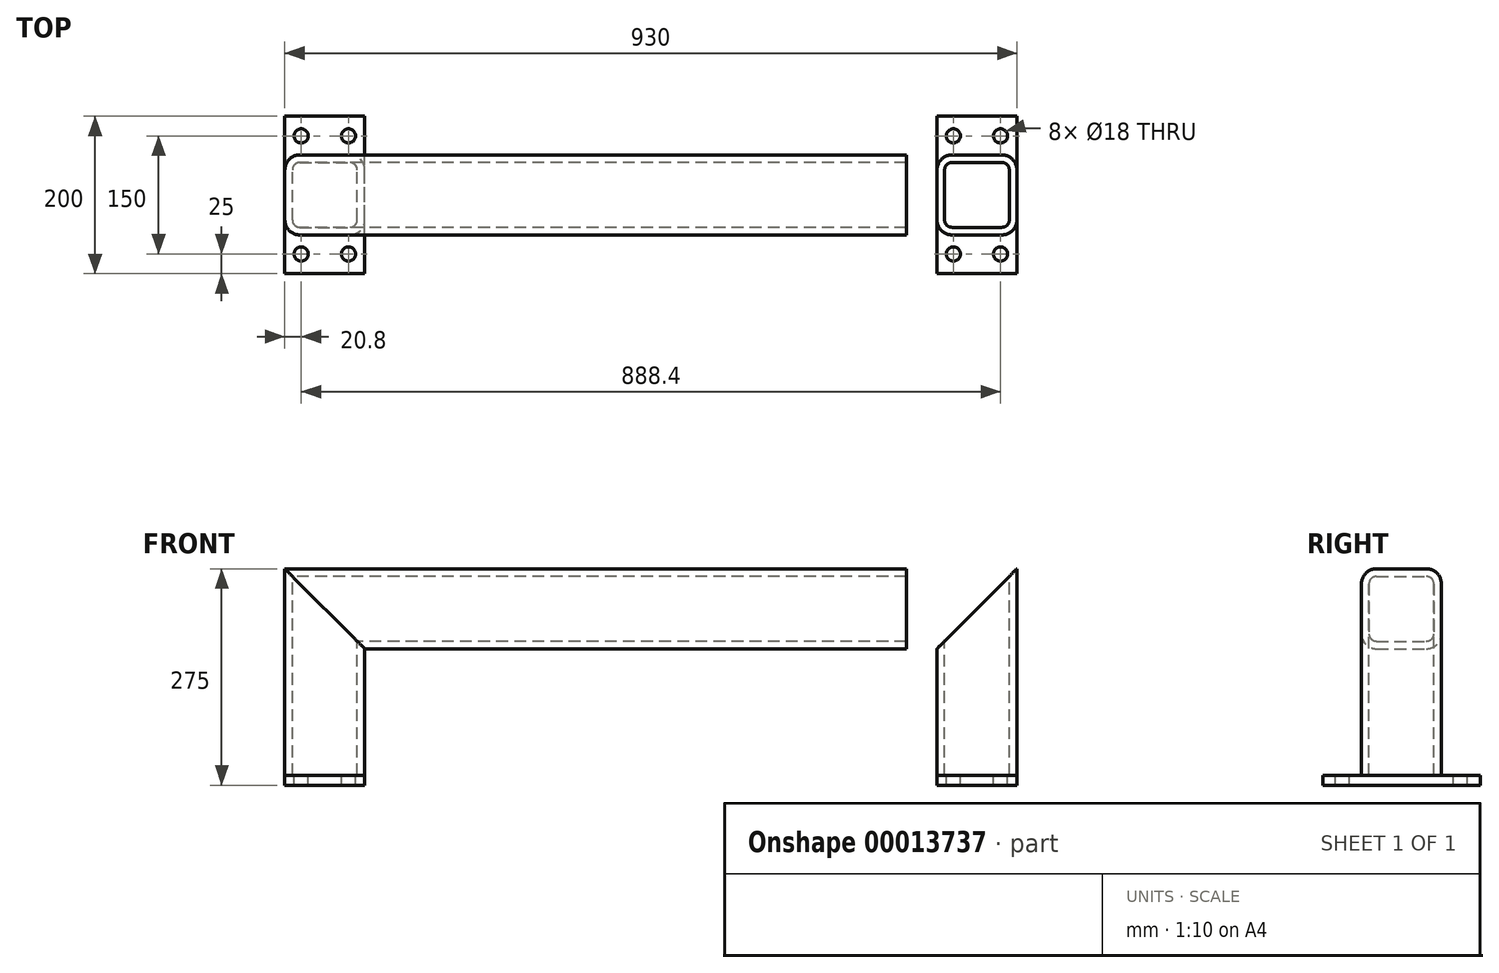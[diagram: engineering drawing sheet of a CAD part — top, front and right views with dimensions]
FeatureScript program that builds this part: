
annotation { "Feature Type Name" : "Feature", "Feature Type Description" : "" }
export const myFeature = defineFeature(function(context is Context, id is Id, definition is map)
    precondition{}
    {
        {
            var Q0;
            Q0=qCreatedBy(makeId("Right.planeOp"),FACE);
            var sketch = newSketch(context, id + "F0", { "sketchPlane" : qUnion([Q0])});
            skLineSegment(sketch, "E0.rect.bottom", {"start": v(-31.8, 50.8) * mm, "end": v(31.8, 50.8) * mm});
            skLineSegment(sketch, "E0.rect.top", {"start": v(-31.8, -50.8) * mm, "end": v(31.8, -50.8) * mm});
            skLineSegment(sketch, "E0.rect.left", {"start": v(-50.8, 31.8) * mm, "end": v(-50.8, -31.8) * mm});
            skLineSegment(sketch, "E0.rect.right", {"start": v(50.8, 31.8) * mm, "end": v(50.8, -31.8) * mm});
            skPoint(sketch, "E0.rect.middle", {"position": v(0, 0) * mm});
            skPoint(sketch, "E1.visualSharp", {"position": v(-50.8, 50.8) * mm});
            skArc(sketch, "E1.filletArc", {"start": v(-31.8, 50.8) * mm, "mid": v(-45.24, 45.24) * mm, "end": v(-50.8, 31.8) * mm});
            skPoint(sketch, "E2.visualSharp", {"position": v(50.8, 50.8) * mm});
            skArc(sketch, "E2.filletArc", {"start": v(50.8, 31.8) * mm, "mid": v(45.24, 45.24) * mm, "end": v(31.8, 50.8) * mm});
            skPoint(sketch, "E3.visualSharp", {"position": v(50.8, -50.8) * mm});
            skArc(sketch, "E3.filletArc", {"start": v(31.8, -50.8) * mm, "mid": v(45.24, -45.24) * mm, "end": v(50.8, -31.8) * mm});
            skPoint(sketch, "E4.visualSharp", {"position": v(-50.8, -50.8) * mm});
            skArc(sketch, "E4.filletArc", {"start": v(-50.8, -31.8) * mm, "mid": v(-45.24, -45.24) * mm, "end": v(-31.8, -50.8) * mm});
            skArc(sketch, "E5.0", {"start": v(-31.8, 41.15) * mm, "mid": v(-38.41, 38.41) * mm, "end": v(-41.15, 31.8) * mm});
            skLineSegment(sketch, "E5.1", {"start": v(-41.15, 31.8) * mm, "end": v(-41.15, -31.8) * mm});
            skArc(sketch, "E5.2", {"start": v(-41.15, -31.8) * mm, "mid": v(-38.41, -38.41) * mm, "end": v(-31.8, -41.15) * mm});
            skLineSegment(sketch, "E5.3", {"start": v(-31.8, -41.15) * mm, "end": v(31.8, -41.15) * mm});
            skArc(sketch, "E5.4", {"start": v(31.8, -41.15) * mm, "mid": v(38.41, -38.41) * mm, "end": v(41.15, -31.8) * mm});
            skLineSegment(sketch, "E5.5", {"start": v(-31.8, 41.15) * mm, "end": v(31.8, 41.15) * mm});
            skLineSegment(sketch, "E5.6", {"start": v(41.15, 31.8) * mm, "end": v(41.15, -31.8) * mm});
            skArc(sketch, "E5.7", {"start": v(41.15, 31.8) * mm, "mid": v(38.41, 38.41) * mm, "end": v(31.8, 41.15) * mm});
            skSolve(sketch);
        }
        {
            var Q0;
            Q0=qSketchRegion(id+"F0",true);
            extrude(context, id + "F1", {"entities" : qUnion([Q0]), "endBound" : BoundingType.SYMMETRIC, "depth" : 930 * mm});
        }
        {
            var Q0;
            Q0=makeQuery(id+"F1.opExtrude","SWEPT_FACE",FACE,{"disambiguationData":[OSD([sQuery(id+"F0.wireOp",EDGE,"E0.rect.right")])]});
            var sketch = newSketch(context, id + "F2", { "sketchPlane" : qUnion([Q0])});
            skLineSegment(sketch, "E6.0", {"start": v(-465, 50.8) * mm, "end": v(465, 50.8) * mm, "construction": true});
            skLineSegment(sketch, "E7.0", {"start": v(-465, -50.8) * mm, "end": v(465, -50.8) * mm, "construction": true});
            skLineSegment(sketch, "E8", {"start": v(-465, 50.8) * mm, "end": v(-337.27, -76.93) * mm});
            skLineSegment(sketch, "E9.0", {"start": v(-465, 31.8) * mm, "end": v(-465, -31.8) * mm});
            skLineSegment(sketch, "E10", {"start": v(-337.27, -76.93) * mm, "end": v(-465, -76.93) * mm});
            skLineSegment(sketch, "E11", {"start": v(-465, -76.93) * mm, "end": v(-465, 50.8) * mm});
            skLineSegment(sketch, "E12", {"start": v(0, 0) * mm, "end": v(0, -179.73) * mm, "construction": true});
            skLineSegment(sketch, "E13.0.MirrorCS", {"start": v(465, -76.93) * mm, "end": v(465, 50.8) * mm});
            skLineSegment(sketch, "E13.1.MirrorCS", {"start": v(465, 50.8) * mm, "end": v(337.27, -76.93) * mm});
            skLineSegment(sketch, "E13.2.MirrorCS", {"start": v(465, 31.8) * mm, "end": v(465, -31.8) * mm});
            skLineSegment(sketch, "E13.3.MirrorCS", {"start": v(337.27, -76.93) * mm, "end": v(465, -76.93) * mm});
            skSolve(sketch);
        }
        {
            var Q0;
            Q0=qSketchRegion(id+"F2",true);
            extrude(context, id + "F3", {"entities" : qUnion([Q0]), "operationType" : NewBodyOperationType.REMOVE, "endBound" : BoundingType.THROUGH_ALL, "oppositeDirection" : true, "depth" : 25 * mm});
        }
        {
            var Q0;
            Q0=makeQuery(id+"F1.opExtrude","SWEPT_FACE",FACE,{"disambiguationData":[OSD([sQuery(id+"F0.wireOp",EDGE,"E0.rect.bottom")])]});
            var sketch = newSketch(context, id + "F4", { "sketchPlane" : qUnion([Q0])});
            skLineSegment(sketch, "E14.0", {"start": v(465, -31.8) * mm, "end": v(465, 31.8) * mm});
            skArc(sketch, "E15.0", {"start": v(465, -31.8) * mm, "mid": v(459.44, -45.24) * mm, "end": v(446, -50.8) * mm});
            skArc(sketch, "E16.0", {"start": v(382.4, -50.8) * mm, "mid": v(368.96, -45.24) * mm, "end": v(363.4, -31.8) * mm});
            skLineSegment(sketch, "E17.0", {"start": v(363.4, -31.8) * mm, "end": v(363.4, 31.8) * mm});
            skArc(sketch, "E18.0", {"start": v(363.4, 31.8) * mm, "mid": v(368.96, 45.24) * mm, "end": v(382.4, 50.8) * mm});
            skArc(sketch, "E19.0", {"start": v(446, 50.8) * mm, "mid": v(459.44, 45.24) * mm, "end": v(465, 31.8) * mm});
            skArc(sketch, "E20.0", {"start": v(446, 41.15) * mm, "mid": v(452.61, 38.41) * mm, "end": v(455.35, 31.8) * mm});
            skLineSegment(sketch, "E21.0", {"start": v(455.35, -31.8) * mm, "end": v(455.35, 31.8) * mm});
            skArc(sketch, "E22.0", {"start": v(455.35, -31.8) * mm, "mid": v(452.61, -38.41) * mm, "end": v(446, -41.15) * mm});
            skArc(sketch, "E23.0", {"start": v(382.4, -41.15) * mm, "mid": v(375.79, -38.41) * mm, "end": v(373.05, -31.8) * mm});
            skLineSegment(sketch, "E24.0", {"start": v(373.05, -31.8) * mm, "end": v(373.05, 31.8) * mm});
            skArc(sketch, "E25.0", {"start": v(373.05, 31.8) * mm, "mid": v(375.79, 38.41) * mm, "end": v(382.4, 41.15) * mm});
            skLineSegment(sketch, "E26", {"start": v(446, -50.8) * mm, "end": v(382.4, -50.8) * mm});
            skLineSegment(sketch, "E27", {"start": v(446, -41.15) * mm, "end": v(382.4, -41.15) * mm});
            skLineSegment(sketch, "E28", {"start": v(446, 41.15) * mm, "end": v(382.4, 41.15) * mm});
            skLineSegment(sketch, "E29", {"start": v(446, 50.8) * mm, "end": v(382.4, 50.8) * mm});
            skSolve(sketch);
        }
        {
            var Q0;
            Q0=qSketchRegion(id+"F4",true);
            extrude(context, id + "F5", {"entities" : qUnion([Q0]), "oppositeDirection" : true, "depth" : (275 - 12.7) * mm});
        }
        {
            var Q0;
            Q0=makeQuery(id+"F5.opExtrude","SWEPT_FACE",FACE,{"disambiguationData":[OSD([sQuery(id+"F4.wireOp",EDGE,"E29")])]});
            var sketch = newSketch(context, id + "F6", { "sketchPlane" : qUnion([Q0])});
            skLineSegment(sketch, "E30.0", {"start": v(-446, 50.8) * mm, "end": v(-465, 50.8) * mm, "construction": true});
            skLineSegment(sketch, "E31.0", {"start": v(-446, 50.8) * mm, "end": v(-382.4, 50.8) * mm, "construction": true});
            skLineSegment(sketch, "E32.0", {"start": v(-363.4, 50.8) * mm, "end": v(-382.4, 50.8) * mm, "construction": true});
            skLineSegment(sketch, "E33.0", {"start": v(-465, -211.5) * mm, "end": v(-465, 50.8) * mm, "construction": true});
            skLineSegment(sketch, "E34.0", {"start": v(-363.4, -211.5) * mm, "end": v(-363.4, 50.8) * mm, "construction": true});
            skLineSegment(sketch, "E35", {"start": v(-465, 50.8) * mm, "end": v(-324.53, -89.67) * mm});
            skLineSegment(sketch, "E36", {"start": v(-324.53, -89.67) * mm, "end": v(-324.53, 50.8) * mm});
            skLineSegment(sketch, "E37", {"start": v(-324.53, 50.8) * mm, "end": v(-465, 50.8) * mm});
            skSolve(sketch);
        }
        {
            var Q0;
            Q0=qSketchRegion(id+"F6",true);
            extrude(context, id + "F7", {"entities" : qUnion([Q0]), "operationType" : NewBodyOperationType.REMOVE, "endBound" : BoundingType.THROUGH_ALL, "oppositeDirection" : true, "depth" : 25 * mm});
        }
        {
            var Q0;
            Q0=makeQuery(id+"F5.opExtrude","SWEPT_BODY",BODY,{"disambiguationData":[OSD([sQuery(id+"F4.wireOp",EDGE,"E14.0"),sQuery(id+"F4.wireOp",EDGE,"E15.0"),sQuery(id+"F4.wireOp",EDGE,"E16.0"),sQuery(id+"F4.wireOp",EDGE,"E17.0"),sQuery(id+"F4.wireOp",EDGE,"E18.0"),sQuery(id+"F4.wireOp",EDGE,"E19.0"),sQuery(id+"F4.wireOp",EDGE,"E20.0"),sQuery(id+"F4.wireOp",EDGE,"E21.0"),sQuery(id+"F4.wireOp",EDGE,"E22.0"),sQuery(id+"F4.wireOp",EDGE,"E23.0"),sQuery(id+"F4.wireOp",EDGE,"E24.0"),sQuery(id+"F4.wireOp",EDGE,"E25.0"),sQuery(id+"F4.wireOp",EDGE,"E26"),sQuery(id+"F4.wireOp",EDGE,"E27"),sQuery(id+"F4.wireOp",EDGE,"E28"),sQuery(id+"F4.wireOp",EDGE,"E29")])]});
            var Q1;
            Q1=qCreatedBy(makeId("Right.planeOp"),FACE);
            mirror(context, id + "F8", {"entities" : qUnion([Q0]), "mirrorPlane" : qUnion([Q1])});
        }
        {
            var Q0;
            Q0=makeQuery(id+"F5.opExtrude","CAP_FACE",FACE,{"disambiguationData":[OSD([sQuery(id+"F4.wireOp",EDGE,"E14.0"),sQuery(id+"F4.wireOp",EDGE,"E15.0"),sQuery(id+"F4.wireOp",EDGE,"E16.0"),sQuery(id+"F4.wireOp",EDGE,"E17.0"),sQuery(id+"F4.wireOp",EDGE,"E18.0"),sQuery(id+"F4.wireOp",EDGE,"E19.0"),sQuery(id+"F4.wireOp",EDGE,"E20.0"),sQuery(id+"F4.wireOp",EDGE,"E21.0"),sQuery(id+"F4.wireOp",EDGE,"E22.0"),sQuery(id+"F4.wireOp",EDGE,"E23.0"),sQuery(id+"F4.wireOp",EDGE,"E24.0"),sQuery(id+"F4.wireOp",EDGE,"E25.0"),sQuery(id+"F4.wireOp",EDGE,"E26"),sQuery(id+"F4.wireOp",EDGE,"E27"),sQuery(id+"F4.wireOp",EDGE,"E28"),sQuery(id+"F4.wireOp",EDGE,"E29")])],"isStart":false});
            var sketch = newSketch(context, id + "F9", { "sketchPlane" : qUnion([Q0])});
            skLineSegment(sketch, "E38", {"start": v(414.2, -100) * mm, "end": v(414.2, 100) * mm, "construction": true});
            skLineSegment(sketch, "E39", {"start": v(465, 0) * mm, "end": v(363.4, 0) * mm, "construction": true});
            skLineSegment(sketch, "E40.0", {"start": v(465, -100) * mm, "end": v(363.4, -100) * mm});
            skLineSegment(sketch, "E41.0.MirrorCS", {"start": v(465, 100) * mm, "end": v(363.4, 100) * mm});
            skLineSegment(sketch, "E42", {"start": v(465, -100) * mm, "end": v(465, 100) * mm});
            skLineSegment(sketch, "E43", {"start": v(363.4, 100) * mm, "end": v(363.4, -100) * mm});
            skPoint(sketch, "E44.orphan", {"position": v(414.2, -50.8) * mm});
            skPoint(sketch, "E45.orphan", {"position": v(414.2, 50.8) * mm});
            skLineSegment(sketch, "E46.0", {"start": v(444.2, -102.5) * mm, "end": v(444.2, 102.5) * mm, "construction": true});
            skLineSegment(sketch, "E47.0", {"start": v(450, -75) * mm, "end": v(348.4, -75) * mm, "construction": true});
            skCircle(sketch, "E48", {"center": v(444.2, -75) * mm, "radius": 9 * mm});
            skCircle(sketch, "E49.0.MirrorC", {"center": v(384.2, -75) * mm, "radius": 9 * mm});
            skCircle(sketch, "E50.0.MirrorC", {"center": v(444.2, 75) * mm, "radius": 9 * mm});
            skCircle(sketch, "E51.0.MirrorC", {"center": v(384.2, 75) * mm, "radius": 9 * mm});
            skSolve(sketch);
        }
        {
            var Q0;
            Q0=qSketchRegion(id+"F9",true);
            extrude(context, id + "F10", {"entities" : qUnion([Q0]), "depth" : 12.7 * mm});
        }
        {
            var Q0;
            Q0=makeQuery(id+"F10.opExtrude","SWEPT_BODY",BODY,{"disambiguationData":[OSD([sQuery(id+"F9.wireOp",EDGE,"E40.0"),sQuery(id+"F9.wireOp",EDGE,"E41.0.MirrorCS"),sQuery(id+"F9.wireOp",EDGE,"E42"),sQuery(id+"F9.wireOp",EDGE,"E43"),sQuery(id+"F9.wireOp",EDGE,"E48"),sQuery(id+"F9.wireOp",EDGE,"E49.0.MirrorC"),sQuery(id+"F9.wireOp",EDGE,"E50.0.MirrorC"),sQuery(id+"F9.wireOp",EDGE,"E51.0.MirrorC")])]});
            var Q1;
            Q1=qCreatedBy(makeId("Right.planeOp"),FACE);
            mirror(context, id + "F11", {"entities" : qUnion([Q0]), "mirrorPlane" : qUnion([Q1])});
        }
    });
